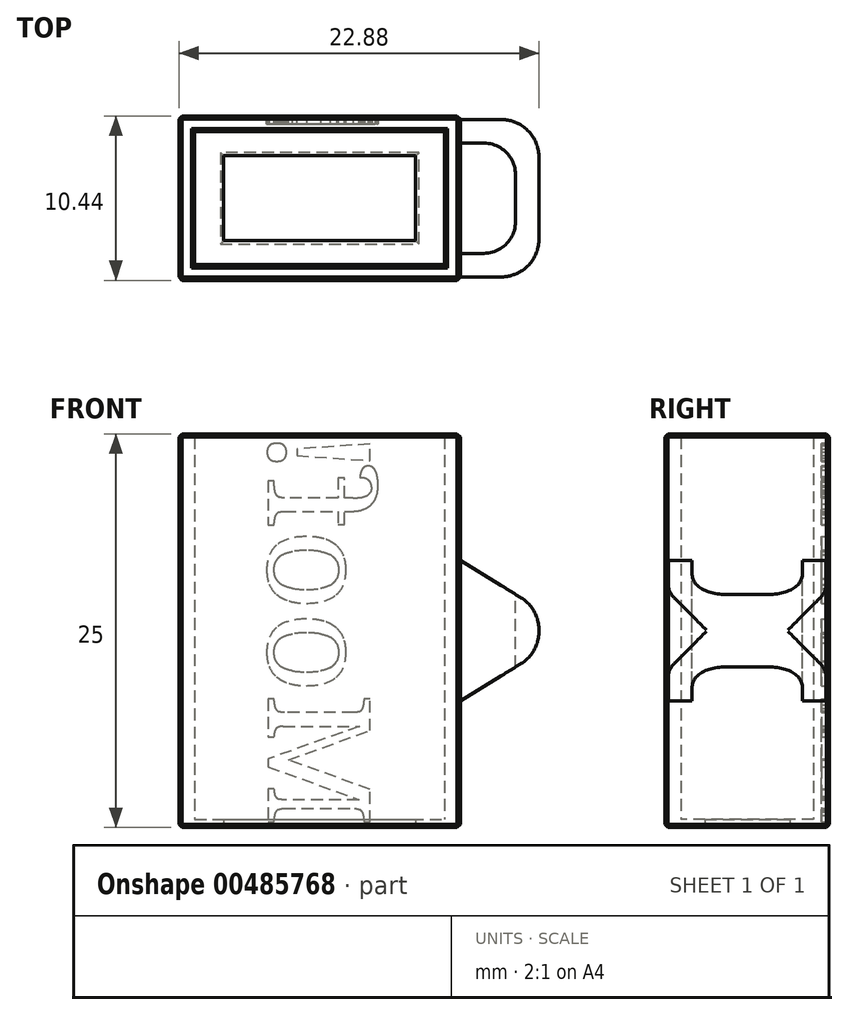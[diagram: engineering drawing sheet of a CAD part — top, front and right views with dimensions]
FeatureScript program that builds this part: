
annotation { "Feature Type Name" : "Feature", "Feature Type Description" : "" }
export const myFeature = defineFeature(function(context is Context, id is Id, definition is map)
    precondition{}
    {
        {
            var Q0;
            Q0=qCreatedBy(makeId("Top.planeOp"),FACE);
            var sketch = newSketch(context, id + "F0", { "sketchPlane" : qUnion([Q0])});
            skLineSegment(sketch, "E0.bottom", {"start": v(0, 8.44) * mm, "end": v(15.88, 8.44) * mm});
            skLineSegment(sketch, "E0.top", {"start": v(0, 0) * mm, "end": v(15.88, 0) * mm});
            skLineSegment(sketch, "E0.left", {"start": v(0, 8.44) * mm, "end": v(0, 0) * mm});
            skLineSegment(sketch, "E0.right", {"start": v(15.88, 8.44) * mm, "end": v(15.88, 0) * mm});
            skLineSegment(sketch, "E1.0", {"start": v(-1, 9.44) * mm, "end": v(16.88, 9.44) * mm});
            skLineSegment(sketch, "E1.1", {"start": v(-1, 9.44) * mm, "end": v(-1, -1) * mm});
            skLineSegment(sketch, "E1.2", {"start": v(-1, -1) * mm, "end": v(16.88, -1) * mm});
            skLineSegment(sketch, "E1.3", {"start": v(16.88, 9.44) * mm, "end": v(16.88, -1) * mm});
            skSolve(sketch);
        }
        {
            var Q0;
            Q0 = qSketchRegion(id + "F0", true);
            extrude(context, id + "F1", {"entities" : qUnion([Q0]), "depth" : 25 * mm});
        }
        {
            var Q0;
            Q0=qCreatedBy(makeId("Top.planeOp"),FACE);
            var sketch = newSketch(context, id + "F2", { "sketchPlane" : qUnion([Q0])});
            skLineSegment(sketch, "E2.bottom", {"start": v(16.88, -1) * mm, "end": v(-1, -1) * mm});
            skLineSegment(sketch, "E2.top", {"start": v(16.88, 9.44) * mm, "end": v(-1, 9.44) * mm});
            skLineSegment(sketch, "E2.left", {"start": v(16.88, -1) * mm, "end": v(16.88, 9.44) * mm});
            skLineSegment(sketch, "E2.right", {"start": v(-1, -1) * mm, "end": v(-1, 9.44) * mm});
            skLineSegment(sketch, "E3.bottom", {"start": v(1.84, 1.52) * mm, "end": v(14.04, 1.52) * mm});
            skLineSegment(sketch, "E3.top", {"start": v(1.84, 6.92) * mm, "end": v(14.04, 6.92) * mm});
            skLineSegment(sketch, "E3.left", {"start": v(1.84, 1.52) * mm, "end": v(1.84, 6.92) * mm});
            skLineSegment(sketch, "E3.right", {"start": v(14.04, 1.52) * mm, "end": v(14.04, 6.92) * mm});
            skPoint(sketch, "E4.startSnap0", {"position": v(7.94, -1) * mm});
            skLineSegment(sketch, "E5", {"start": v(7.94, -1) * mm, "end": v(7.94, 9.44) * mm, "construction": true});
            skLineSegment(sketch, "E6", {"start": v(-1, 4.22) * mm, "end": v(16.24, 4.22) * mm, "construction": true});
            skPoint(sketch, "E6.endSnap0", {"position": v(16.88, 4.22) * mm});
            skSolve(sketch);
        }
        {
            var Q0;
            Q0=makeQuery(id+"F2.imprint","IMPRINT",FACE,{"disambiguationData":[TD([[makeQuery(id+"F2.imprint","IMPRINT",EDGE,{"derivedFrom":sQuery(id+"F2.wireOp",EDGE,"E2.bottom")}),-1.0]])]});
            extrude(context, id + "F3", {"entities" : qUnion([Q0]), "operationType" : NewBodyOperationType.ADD, "depth" : .5 * mm});
        }
        {
            var Q0;
            Q0=makeQuery(id+"F1.opExtrude","SWEPT_EDGE",EDGE,{"disambiguationData":[OSD([sQuery(id+"F0.wireOp",EDGE,"E1.1"),sQuery(id+"F0.wireOp",EDGE,"E1.2")])]});
            cPoint(context, id + "F4", {"entities" : qUnion([Q0]), "parameter" : 0.5});
        }
        {
            var Q0;
            Q0=makeQuery(id+"F1.opExtrude","SWEPT_EDGE",EDGE,{"disambiguationData":[OSD([sQuery(id+"F0.wireOp",EDGE,"E1.0"),sQuery(id+"F0.wireOp",EDGE,"E1.1")])]});
            cPoint(context, id + "F5", {"entities" : qUnion([Q0]), "parameter" : 0.5});
        }
        {
            var Q0;
            Q0=makeQuery(id+"F1.opExtrude","SWEPT_EDGE",EDGE,{"disambiguationData":[OSD([sQuery(id+"F0.wireOp",EDGE,"E1.0"),sQuery(id+"F0.wireOp",EDGE,"E1.3")])]});
            cPoint(context, id + "F6", {"entities" : qUnion([Q0]), "parameter" : 0.5});
        }
        {
            var Q0;
            Q0 = qCreatedBy(id + "F4" ,VERTEX);
            var Q1;
            Q1 = qCreatedBy(id + "F5" ,VERTEX);
            var Q2;
            Q2 = qCreatedBy(id + "F6" ,VERTEX);
            cPlane(context, id + "F7", {"entities" : qUnion([Q0, Q1, Q2]), "cplaneType" : CPlaneType.THREE_POINT, "offset" : 25 * mm, "width" : 150 * mm, "height" : 150 * mm});
        }
        {
            var Q0;
            Q0=qCreatedBy(id+"F7.planeOp",FACE);
            var sketch = newSketch(context, id + "F8", { "sketchPlane" : qUnion([Q0])});
            skArc(sketch, "E7", {"start": v(16.88, -0.8) * mm, "mid": v(21.9, 4.22) * mm, "end": v(16.88, 9.24) * mm});
            skArc(sketch, "E8.0", {"start": v(16.88, 1.2) * mm, "mid": v(19.9, 4.22) * mm, "end": v(16.88, 7.24) * mm});
            skLineSegment(sketch, "E9", {"start": v(16.88, 9.24) * mm, "end": v(16.88, 7.24) * mm});
            skLineSegment(sketch, "E10", {"start": v(16.88, 1.2) * mm, "end": v(16.88, -0.8) * mm});
            skSolve(sketch);
        }
        {
            var Q0;
            Q0 = qSketchRegion(id + "F8", true);
            extrude(context, id + "F9", {"entities" : qUnion([Q0]), "endBound" : BoundingType.SYMMETRIC, "depth" : 2 * mm});
        }
        {
            var Q0;
            Q0=makeQuery(id+"F9.opExtrude","CAP_EDGE",EDGE,{"disambiguationData":[OSD([sQuery(id+"F8.wireOp",EDGE,"k7BCvRtP-n6ig-QiNF-fAq4-0sCIjOex6o2M")])],"isStart":false});
            var Q1;
            Q1=makeQuery(id+"F9.opExtrude","CAP_EDGE",EDGE,{"disambiguationData":[OSD([sQuery(id+"F8.wireOp",EDGE,"279694ad-2ed9-4ee1-85d5-d3006be54f8f.0")])],"isStart":false});
            var Q2;
            Q2=makeQuery(id+"F9.opExtrude","CAP_EDGE",EDGE,{"disambiguationData":[OSD([sQuery(id+"F8.wireOp",EDGE,"279694ad-2ed9-4ee1-85d5-d3006be54f8f.0")])],"isStart":true});
            var Q3;
            Q3=makeQuery(id+"F9.opExtrude","CAP_EDGE",EDGE,{"disambiguationData":[OSD([sQuery(id+"F8.wireOp",EDGE,"k7BCvRtP-n6ig-QiNF-fAq4-0sCIjOex6o2M")])],"isStart":true});
            var Q4;
            Q4=makeQuery(id+"F9.opExtrude","CAP_EDGE",EDGE,{"disambiguationData":[OSD([sQuery(id+"F8.wireOp",EDGE,"NvVtK32R-sKu6-8KPA-j12X-PsLzZPmmVvWm")])],"isStart":true});
            var Q5;
            Q5=makeQuery(id+"F9.opExtrude","CAP_EDGE",EDGE,{"disambiguationData":[OSD([sQuery(id+"F8.wireOp",EDGE,"974c9f8a-bdd2-4d0b-b1f6-060c271b1fca.0")])],"isStart":true});
            var Q6;
            Q6=makeQuery(id+"F9.opExtrude","CAP_EDGE",EDGE,{"disambiguationData":[OSD([sQuery(id+"F8.wireOp",EDGE,"NvVtK32R-sKu6-8KPA-j12X-PsLzZPmmVvWm")])],"isStart":false});
            var Q7;
            Q7=makeQuery(id+"F9.opExtrude","CAP_EDGE",EDGE,{"disambiguationData":[OSD([sQuery(id+"F8.wireOp",EDGE,"974c9f8a-bdd2-4d0b-b1f6-060c271b1fca.0")])],"isStart":false});
            var Q8;
            Q8=makeQuery(id+"F9.opExtrude","CAP_EDGE",EDGE,{"disambiguationData":[OSD([sQuery(id+"F8.wireOp",EDGE,"E8.0")])],"isStart":false});
            var Q9;
            Q9=makeQuery(id+"F9.opExtrude","CAP_EDGE",EDGE,{"disambiguationData":[OSD([sQuery(id+"F8.wireOp",EDGE,"E7")])],"isStart":false});
            var Q10;
            Q10=makeQuery(id+"F9.opExtrude","CAP_EDGE",EDGE,{"disambiguationData":[OSD([sQuery(id+"F8.wireOp",EDGE,"E7")])],"isStart":true});
            var Q11;
            Q11=makeQuery(id+"F9.opExtrude","CAP_EDGE",EDGE,{"disambiguationData":[OSD([sQuery(id+"F8.wireOp",EDGE,"E8.0")])],"isStart":true});
            fillet(context, id + "F10", {"entities" : qUnion([Q0, Q1, Q2, Q3, Q4, Q5, Q6, Q7, Q8, Q9, Q10, Q11]), "radius" : 1 * mm, "tangentPropagation" : true, "allowEdgeOverflow" : false});
        }
        {
            var Q0;
            Q0=makeQuery(id+"F1.opExtrude","SWEPT_FACE",FACE,{"disambiguationData":[OSD([sQuery(id+"F0.wireOp",EDGE,"E1.0")])]});
            var sketch = newSketch(context, id + "F11", { "sketchPlane" : qUnion([Q0])});
            skText(sketch, "E11", { "text": "Moof!", "fontName": "NotoSerif-Regular.ttf"});
            skLineSegment(sketch, "E12", {"start": v(-7.94, 25) * mm, "end": v(-7.94, 0) * mm, "construction": true});
            skLineSegment(sketch, "E13", {"start": v(1, 12.5) * mm, "end": v(-16.88, 12.5) * mm, "construction": true});
            const initialGuessF11  = {"E11": [-0.00467, 0, 0, 1, 0.00653]};
            skSetInitialGuess(sketch, initialGuessF11);
            skSolve(sketch);
        }
        {
            var Q0;
            Q0 = qSketchRegion(id + "F11", true);
            extrude(context, id + "F12", {"entities" : qUnion([Q0]), "operationType" : NewBodyOperationType.REMOVE, "oppositeDirection" : true, "depth" : .5 * mm});
        }
        {
            var Q0;
            Q0=makeQuery(id+"F3.boolean.opBoolean","MERGE",FACE,{"derivedFrom":[makeQuery(id+"F1.opExtrude","CAP_FACE",FACE,{"disambiguationData":[OSD([sQuery(id+"F0.wireOp",EDGE,"E0.bottom"),sQuery(id+"F0.wireOp",EDGE,"E0.top"),sQuery(id+"F0.wireOp",EDGE,"E0.left"),sQuery(id+"F0.wireOp",EDGE,"E0.right"),sQuery(id+"F0.wireOp",EDGE,"E1.0"),sQuery(id+"F0.wireOp",EDGE,"E1.1"),sQuery(id+"F0.wireOp",EDGE,"E1.2"),sQuery(id+"F0.wireOp",EDGE,"E1.3")])],"isStart":true}),makeQuery(id+"F3.opExtrude","CAP_FACE",FACE,{"disambiguationData":[OSD([sQuery(id+"F2.wireOp",EDGE,"E2.bottom"),sQuery(id+"F2.wireOp",EDGE,"E2.top"),sQuery(id+"F2.wireOp",EDGE,"E2.left"),sQuery(id+"F2.wireOp",EDGE,"E2.right"),sQuery(id+"F2.wireOp",EDGE,"E3.bottom"),sQuery(id+"F2.wireOp",EDGE,"E3.top"),sQuery(id+"F2.wireOp",EDGE,"E3.left"),sQuery(id+"F2.wireOp",EDGE,"E3.right")])],"isStart":true})]});
            var Q1;
            Q1=makeQuery(id+"F1.opExtrude","CAP_FACE",FACE,{"disambiguationData":[OSD([sQuery(id+"F0.wireOp",EDGE,"E0.bottom"),sQuery(id+"F0.wireOp",EDGE,"E0.top"),sQuery(id+"F0.wireOp",EDGE,"E0.left"),sQuery(id+"F0.wireOp",EDGE,"E0.right"),sQuery(id+"F0.wireOp",EDGE,"E1.0"),sQuery(id+"F0.wireOp",EDGE,"E1.1"),sQuery(id+"F0.wireOp",EDGE,"E1.2"),sQuery(id+"F0.wireOp",EDGE,"E1.3")])],"isStart":false});
            var Q2;
            Q2=makeQuery(id+"F1.opExtrude","SWEPT_FACE",FACE,{"disambiguationData":[OSD([sQuery(id+"F0.wireOp",EDGE,"E1.1")])]});
            var Q3;
            Q3=makeQuery(id+"F1.opExtrude","SWEPT_FACE",FACE,{"disambiguationData":[OSD([sQuery(id+"F0.wireOp",EDGE,"E1.3")])]});
            chamfer(context, id + "F13", {"entities" : qUnion([Q0, Q1, Q2, Q3]), "width" : 0.2 * mm, "tangentPropagation" : true});
        }
        {
            var Q0;
            {var subQ0=sQuery(id+"F0.wireOp",EDGE,"E1.1");Q0=makeQuery(id+"F13.opChamfer","BLEND_EDGE",EDGE,{"blendedFrom":[makeQuery(id+"F1.opExtrude","CAP_EDGE",EDGE,{"disambiguationData":[OSD([subQ0])],"isStart":true}),makeQuery(id+"F3.boolean.opBoolean","MERGE",FACE,{"derivedFrom":[makeQuery(id+"F1.opExtrude","CAP_FACE",FACE,{"disambiguationData":[OSD([sQuery(id+"F0.wireOp",EDGE,"E0.bottom"),sQuery(id+"F0.wireOp",EDGE,"E0.top"),sQuery(id+"F0.wireOp",EDGE,"E0.left"),sQuery(id+"F0.wireOp",EDGE,"E0.right"),sQuery(id+"F0.wireOp",EDGE,"E1.0"),subQ0,sQuery(id+"F0.wireOp",EDGE,"E1.2"),sQuery(id+"F0.wireOp",EDGE,"E1.3")])],"isStart":true}),makeQuery(id+"F3.opExtrude","CAP_FACE",FACE,{"disambiguationData":[OSD([sQuery(id+"F2.wireOp",EDGE,"E2.bottom"),sQuery(id+"F2.wireOp",EDGE,"E2.top"),sQuery(id+"F2.wireOp",EDGE,"E2.left"),sQuery(id+"F2.wireOp",EDGE,"E2.right"),sQuery(id+"F2.wireOp",EDGE,"E3.bottom"),sQuery(id+"F2.wireOp",EDGE,"E3.top"),sQuery(id+"F2.wireOp",EDGE,"E3.left"),sQuery(id+"F2.wireOp",EDGE,"E3.right")])],"isStart":true})]})],"blendedInto":[makeQuery(id+"F3.boolean.opBoolean","MERGE",FACE,{"derivedFrom":[makeQuery(id+"F1.opExtrude","CAP_FACE",FACE,{"disambiguationData":[OSD([sQuery(id+"F0.wireOp",EDGE,"E0.bottom"),sQuery(id+"F0.wireOp",EDGE,"E0.top"),sQuery(id+"F0.wireOp",EDGE,"E0.left"),sQuery(id+"F0.wireOp",EDGE,"E0.right"),sQuery(id+"F0.wireOp",EDGE,"E1.0"),subQ0,sQuery(id+"F0.wireOp",EDGE,"E1.2"),sQuery(id+"F0.wireOp",EDGE,"E1.3")])],"isStart":true}),makeQuery(id+"F3.opExtrude","CAP_FACE",FACE,{"disambiguationData":[OSD([sQuery(id+"F2.wireOp",EDGE,"E2.bottom"),sQuery(id+"F2.wireOp",EDGE,"E2.top"),sQuery(id+"F2.wireOp",EDGE,"E2.left"),sQuery(id+"F2.wireOp",EDGE,"E2.right"),sQuery(id+"F2.wireOp",EDGE,"E3.bottom"),sQuery(id+"F2.wireOp",EDGE,"E3.top"),sQuery(id+"F2.wireOp",EDGE,"E3.left"),sQuery(id+"F2.wireOp",EDGE,"E3.right")])],"isStart":true})]})]});}
            cPoint(context, id + "F14", {"entities" : qUnion([Q0]), "parameter" : 0.5});
        }
        {
            var Q0;
            {var subQ0=sQuery(id+"F0.wireOp",EDGE,"E1.3");Q0=makeQuery(id+"F13.opChamfer","BLEND_EDGE",EDGE,{"blendedFrom":[makeQuery(id+"F1.opExtrude","CAP_EDGE",EDGE,{"disambiguationData":[OSD([subQ0])],"isStart":true}),makeQuery(id+"F3.boolean.opBoolean","MERGE",FACE,{"derivedFrom":[makeQuery(id+"F1.opExtrude","CAP_FACE",FACE,{"disambiguationData":[OSD([sQuery(id+"F0.wireOp",EDGE,"E0.bottom"),sQuery(id+"F0.wireOp",EDGE,"E0.top"),sQuery(id+"F0.wireOp",EDGE,"E0.left"),sQuery(id+"F0.wireOp",EDGE,"E0.right"),sQuery(id+"F0.wireOp",EDGE,"E1.0"),sQuery(id+"F0.wireOp",EDGE,"E1.1"),sQuery(id+"F0.wireOp",EDGE,"E1.2"),subQ0])],"isStart":true}),makeQuery(id+"F3.opExtrude","CAP_FACE",FACE,{"disambiguationData":[OSD([sQuery(id+"F2.wireOp",EDGE,"E2.bottom"),sQuery(id+"F2.wireOp",EDGE,"E2.top"),sQuery(id+"F2.wireOp",EDGE,"E2.left"),sQuery(id+"F2.wireOp",EDGE,"E2.right"),sQuery(id+"F2.wireOp",EDGE,"E3.bottom"),sQuery(id+"F2.wireOp",EDGE,"E3.top"),sQuery(id+"F2.wireOp",EDGE,"E3.left"),sQuery(id+"F2.wireOp",EDGE,"E3.right")])],"isStart":true})]})],"blendedInto":[makeQuery(id+"F3.boolean.opBoolean","MERGE",FACE,{"derivedFrom":[makeQuery(id+"F1.opExtrude","CAP_FACE",FACE,{"disambiguationData":[OSD([sQuery(id+"F0.wireOp",EDGE,"E0.bottom"),sQuery(id+"F0.wireOp",EDGE,"E0.top"),sQuery(id+"F0.wireOp",EDGE,"E0.left"),sQuery(id+"F0.wireOp",EDGE,"E0.right"),sQuery(id+"F0.wireOp",EDGE,"E1.0"),sQuery(id+"F0.wireOp",EDGE,"E1.1"),sQuery(id+"F0.wireOp",EDGE,"E1.2"),subQ0])],"isStart":true}),makeQuery(id+"F3.opExtrude","CAP_FACE",FACE,{"disambiguationData":[OSD([sQuery(id+"F2.wireOp",EDGE,"E2.bottom"),sQuery(id+"F2.wireOp",EDGE,"E2.top"),sQuery(id+"F2.wireOp",EDGE,"E2.left"),sQuery(id+"F2.wireOp",EDGE,"E2.right"),sQuery(id+"F2.wireOp",EDGE,"E3.bottom"),sQuery(id+"F2.wireOp",EDGE,"E3.top"),sQuery(id+"F2.wireOp",EDGE,"E3.left"),sQuery(id+"F2.wireOp",EDGE,"E3.right")])],"isStart":true})]})]});}
            cPoint(context, id + "F15", {"entities" : qUnion([Q0]), "parameter" : 0.5});
        }
        {
            var Q0;
            {var subQ0=sQuery(id+"F0.wireOp",EDGE,"E0.left");Q0=makeQuery(id+"F13.opChamfer","BLEND_EDGE",EDGE,{"blendedFrom":[makeQuery(id+"F1.opExtrude","CAP_EDGE",EDGE,{"disambiguationData":[OSD([subQ0])],"isStart":false}),makeQuery(id+"F1.opExtrude","SWEPT_FACE",FACE,{"disambiguationData":[OSD([subQ0])]})],"blendedInto":[makeQuery(id+"F1.opExtrude","SWEPT_FACE",FACE,{"disambiguationData":[OSD([subQ0])]})]});}
            cPoint(context, id + "F16", {"entities" : qUnion([Q0]), "parameter" : 0.5});
        }
        {
            var Q0;
            Q0 = qCreatedBy(id + "F14" ,VERTEX);
            var Q1;
            Q1 = qCreatedBy(id + "F15" ,VERTEX);
            var Q2;
            Q2 = qCreatedBy(id + "F16" ,VERTEX);
            cPlane(context, id + "F17", {"entities" : qUnion([Q0, Q1, Q2]), "cplaneType" : CPlaneType.THREE_POINT, "offset" : 25 * mm, "width" : 150 * mm, "height" : 150 * mm});
        }
        {
            var Q0;
            Q0=qCreatedBy(id+"F17.planeOp",FACE);
            var sketch = newSketch(context, id + "F18", { "sketchPlane" : qUnion([Q0])});
            skLineSegment(sketch, "E14", {"start": v(-16.88, 16.98) * mm, "end": v(-21.88, 13.88) * mm});
            skLineSegment(sketch, "E15", {"start": v(-21.88, 13.88) * mm, "end": v(-21.88, 11.12) * mm});
            skLineSegment(sketch, "E16", {"start": v(-21.88, 11.12) * mm, "end": v(-16.88, 8.02) * mm});
            skLineSegment(sketch, "E17", {"start": v(-16.88, 16.98) * mm, "end": v(-16.88, 8.02) * mm});
            skSolve(sketch);
        }
        {
            var Q0;
            Q0 = qSketchRegion(id + "F18", true);
            extrude(context, id + "F19", {"entities" : qUnion([Q0]), "endBound" : BoundingType.SYMMETRIC, "depth" : 10 * mm});
        }
        {
            var Q0;
            Q0=makeQuery(id+"F19.opExtrude","SWEPT_FACE",FACE,{"disambiguationData":[OSD([sQuery(id+"F18.wireOp",EDGE,"E15")])]});
            fillet(context, id + "F20", {"entities" : qUnion([Q0]), "radius" : 2.42 * mm, "tangentPropagation" : true, "allowEdgeOverflow" : false});
        }
        {
            var Q0;
            Q0=qCreatedBy(id+"F7.planeOp",FACE);
            var sketch = newSketch(context, id + "F21", { "sketchPlane" : qUnion([Q0])});
            skLineSegment(sketch, "E18.bottom", {"start": v(16.88, 0.72) * mm, "end": v(18.38, 0.72) * mm});
            skLineSegment(sketch, "E18.top", {"start": v(16.88, 7.72) * mm, "end": v(18.38, 7.72) * mm});
            skLineSegment(sketch, "E18.left", {"start": v(16.88, 0.72) * mm, "end": v(16.88, 7.72) * mm});
            skLineSegment(sketch, "E18.right", {"start": v(20.38, 2.72) * mm, "end": v(20.38, 5.72) * mm});
            skPoint(sketch, "E19.visualSharp", {"position": v(20.38, 0.72) * mm});
            skArc(sketch, "E19.filletArc", {"start": v(18.38, 0.72) * mm, "mid": v(19.8, 1.3) * mm, "end": v(20.38, 2.72) * mm});
            skPoint(sketch, "E20.visualSharp", {"position": v(20.38, 7.72) * mm});
            skArc(sketch, "E20.filletArc", {"start": v(20.38, 5.72) * mm, "mid": v(19.8, 7.13) * mm, "end": v(18.38, 7.72) * mm});
            skSolve(sketch);
        }
        {
            var Q0;
            Q0 = qSketchRegion(id + "F21", true);
            extrude(context, id + "F22", {"entities" : qUnion([Q0]), "operationType" : NewBodyOperationType.REMOVE, "endBound" : BoundingType.SYMMETRIC, "oppositeDirection" : true, "depth" : 25 * mm});
        }
        {
            var Q0;
            Q0=makeQuery(id+"F9.opExtrude","SWEPT_BODY",BODY,{"disambiguationData":[OSD([sQuery(id+"F8.wireOp",EDGE,"E7"),sQuery(id+"F8.wireOp",EDGE,"E8.0"),sQuery(id+"F8.wireOp",EDGE,"E9"),sQuery(id+"F8.wireOp",EDGE,"E10")])]});
            deleteBodies(context, id + "F23", {"entities" : qUnion([Q0])});
        }
    });
